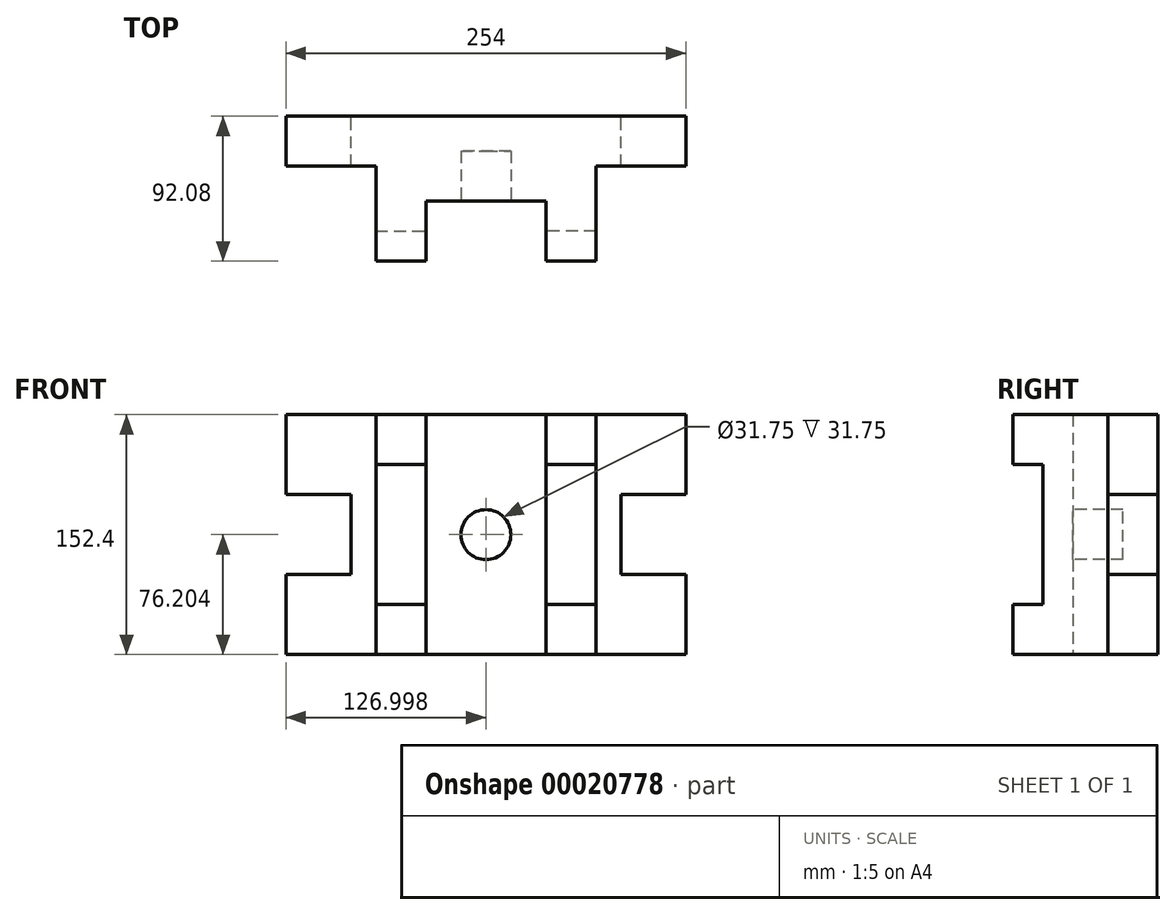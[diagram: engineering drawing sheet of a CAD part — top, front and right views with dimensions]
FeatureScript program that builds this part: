
annotation { "Feature Type Name" : "Feature", "Feature Type Description" : "" }
export const myFeature = defineFeature(function(context is Context, id is Id, definition is map)
    precondition{}
    {
        {
            var Q0;
            Q0=qCreatedBy(makeId("Front.planeOp"),FACE);
            var sketch = newSketch(context, id + "F0", { "sketchPlane" : qUnion([Q0])});
            skLineSegment(sketch, "E0.rect.bottom", {"start": v(31.56, -35.05) * mm, "end": v(-95.44, -35.05) * mm});
            skLineSegment(sketch, "E0.rect.top", {"start": v(-9.72, 41.15) * mm, "end": v(-95.44, 41.15) * mm});
            skLineSegment(sketch, "E0.rect.left", {"start": v(31.56, -35.05) * mm, "end": v(31.56, 15.75) * mm});
            skLineSegment(sketch, "E0.rect.right", {"start": v(-95.44, -35.05) * mm, "end": v(-95.44, 41.15) * mm});
            skPoint(sketch, "E0.rect.middle", {"position": v(-31.94, 3.05) * mm});
            skLineSegment(sketch, "E1.top", {"start": v(31.56, 15.75) * mm, "end": v(-9.72, 15.75) * mm});
            skLineSegment(sketch, "E1.right", {"start": v(-9.72, 41.15) * mm, "end": v(-9.72, 15.75) * mm});
            skPoint(sketch, "E2.orphan", {"position": v(31.56, 41.15) * mm});
            skSolve(sketch);
        }
        {
            var Q0;
            Q0=makeQuery(id+"F0.imprint","IMPRINT",FACE,{"disambiguationData":[TD([[makeQuery(id+"F0.imprint","IMPRINT",EDGE,{"derivedFrom":sQuery(id+"F0.wireOp",EDGE,"E0.rect.bottom")}),-1.0]])]});
            extrude(context, id + "F1", {"entities" : qUnion([Q0]), "depth" : 31.75 * mm});
        }
        {
            var Q0;
            Q0=makeQuery(id+"F1.opExtrude","CAP_FACE",FACE,{"disambiguationData":[OSD([sQuery(id+"F0.wireOp",EDGE,"E0.rect.bottom"),sQuery(id+"F0.wireOp",EDGE,"E0.rect.top"),sQuery(id+"F0.wireOp",EDGE,"E0.rect.left"),sQuery(id+"F0.wireOp",EDGE,"E0.rect.right"),sQuery(id+"F0.wireOp",EDGE,"E1.top"),sQuery(id+"F0.wireOp",EDGE,"E1.right")])],"isStart":false});
            var sketch = newSketch(context, id + "F2", { "sketchPlane" : qUnion([Q0])});
            skLineSegment(sketch, "E3.bottom", {"start": v(-95.44, -35.05) * mm, "end": v(-25.6, -35.05) * mm});
            skLineSegment(sketch, "E3.top", {"start": v(-95.44, 41.15) * mm, "end": v(-25.6, 41.15) * mm});
            skLineSegment(sketch, "E3.left", {"start": v(-95.44, -35.05) * mm, "end": v(-95.44, 41.15) * mm});
            skLineSegment(sketch, "E3.right", {"start": v(-25.6, -35.05) * mm, "end": v(-25.6, 41.15) * mm});
            skLineSegment(sketch, "E4.bottom", {"start": v(-25.6, -35.05) * mm, "end": v(-48.16, -35.05) * mm});
            skLineSegment(sketch, "E4.left", {"start": v(-25.6, -35.05) * mm, "end": v(-25.6, -11.85) * mm});
            skSolve(sketch);
        }
        {
            var Q0;
            Q0=makeQuery(id+"F2.imprint","IMPRINT",FACE,{"disambiguationData":[TD([[makeQuery(id+"F2.imprint","IMPRINT",EDGE,{"derivedFrom":sQuery(id+"F2.wireOp",EDGE,"E3.bottom")}),-1.0]])]});
            extrude(context, id + "F3", {"entities" : qUnion([Q0]), "operationType" : NewBodyOperationType.ADD, "depth" : 60.32 * mm});
        }
        {
            var Q0;
            Q0=makeQuery(id+"F3.opExtrude","CAP_FACE",FACE,{"disambiguationData":[OSD([sQuery(id+"F2.wireOp",EDGE,"E3.bottom"),sQuery(id+"F2.wireOp",EDGE,"E3.top"),sQuery(id+"F2.wireOp",EDGE,"E3.left"),sQuery(id+"F2.wireOp",EDGE,"E3.right"),sQuery(id+"F2.wireOp",EDGE,"E4.bottom"),sQuery(id+"F2.wireOp",EDGE,"E4.left")])],"isStart":false});
            var sketch = newSketch(context, id + "F4", { "sketchPlane" : qUnion([Q0])});
            skLineSegment(sketch, "E5.bottom", {"start": v(-25.6, -35.05) * mm, "end": v(-57.34, -35.05) * mm});
            skLineSegment(sketch, "E5.top", {"start": v(-25.6, -3.3) * mm, "end": v(-57.34, -3.3) * mm});
            skLineSegment(sketch, "E5.left", {"start": v(-25.6, -35.05) * mm, "end": v(-25.6, -3.3) * mm});
            skLineSegment(sketch, "E5.right", {"start": v(-57.34, -35.05) * mm, "end": v(-57.34, -3.3) * mm});
            skLineSegment(sketch, "E6", {"start": v(-57.34, -3.3) * mm, "end": v(-57.34, 41.15) * mm});
            skSolve(sketch);
        }
        {
            var Q0;
            {var subQ4=sQuery(id+"F4.wireOp",EDGE,"E5.top");Q0=makeQuery(id+"F4.imprint","IMPRINT",FACE,{"disambiguationData":[TD([[makeQuery(id+"F4.imprint","IMPRINT",EDGE,{"derivedFrom":subQ4}),-1.0]])]});}
            extrude(context, id + "F5", {"entities" : qUnion([Q0]), "operationType" : NewBodyOperationType.REMOVE, "oppositeDirection" : true, "depth" : 19.05 * mm});
        }
        {
            var Q0;
            Q0=makeQuery(id+"F3.opExtrude","CAP_FACE",FACE,{"disambiguationData":[OSD([sQuery(id+"F2.wireOp",EDGE,"E3.bottom"),sQuery(id+"F2.wireOp",EDGE,"E3.top"),sQuery(id+"F2.wireOp",EDGE,"E3.left"),sQuery(id+"F2.wireOp",EDGE,"E3.right"),sQuery(id+"F2.wireOp",EDGE,"E4.bottom"),sQuery(id+"F2.wireOp",EDGE,"E4.left")])],"isStart":false});
            var sketch = newSketch(context, id + "F6", { "sketchPlane" : qUnion([Q0])});
            skLineSegment(sketch, "E7", {"start": v(-57.34, -3.3) * mm, "end": v(-57.34, -35.05) * mm});
            skSolve(sketch);
        }
        {
            var Q0;
            {var subQ1=sQuery(id+"F6.wireOp",EDGE,"E7");Q0=makeQuery(id+"F6.imprint","IMPRINT",FACE,{"disambiguationData":[TD([[makeQuery(id+"F6.imprint","IMPRINT",EDGE,{"derivedFrom":subQ1}),-1.0]])]});}
            extrude(context, id + "F7", {"entities" : qUnion([Q0]), "operationType" : NewBodyOperationType.REMOVE, "oppositeDirection" : true, "depth" : 38.1 * mm});
        }
        {
            var Q0;
            Q0=makeQuery(id+"F1.opExtrude","SWEPT_BODY",BODY,{"disambiguationData":[OSD([sQuery(id+"F0.wireOp",EDGE,"E0.rect.bottom"),sQuery(id+"F0.wireOp",EDGE,"E0.rect.top"),sQuery(id+"F0.wireOp",EDGE,"E0.rect.left"),sQuery(id+"F0.wireOp",EDGE,"E0.rect.right"),sQuery(id+"F0.wireOp",EDGE,"E1.top"),sQuery(id+"F0.wireOp",EDGE,"E1.right")])]});
            var Q1;
            Q1=makeQuery(id+"F3.boolean.opBoolean","MERGE",FACE,{"derivedFrom":[makeQuery(id+"F1.opExtrude","SWEPT_FACE",FACE,{"disambiguationData":[OSD([sQuery(id+"F0.wireOp",EDGE,"E0.rect.top")])]}),makeQuery(id+"F3.opExtrude","SWEPT_FACE",FACE,{"disambiguationData":[OSD([sQuery(id+"F2.wireOp",EDGE,"E3.top")])]})]});
            mirror(context, id + "F8", {"operationType" : NewBodyOperationType.ADD, "entities" : qUnion([Q0]), "mirrorPlane" : qUnion([Q1])});
        }
        {
            var Q0;
            Q0=makeQuery(id+"F1.opExtrude","SWEPT_BODY",BODY,{"disambiguationData":[OSD([sQuery(id+"F0.wireOp",EDGE,"E0.rect.bottom"),sQuery(id+"F0.wireOp",EDGE,"E0.rect.top"),sQuery(id+"F0.wireOp",EDGE,"E0.rect.left"),sQuery(id+"F0.wireOp",EDGE,"E0.rect.right"),sQuery(id+"F0.wireOp",EDGE,"E1.top"),sQuery(id+"F0.wireOp",EDGE,"E1.right")])]});
            var Q1;
            {var subQ0=makeQuery(id+"F3.boolean.opBoolean","MERGE",FACE,{"derivedFrom":[makeQuery(id+"F1.opExtrude","SWEPT_FACE",FACE,{"disambiguationData":[OSD([sQuery(id+"F0.wireOp",EDGE,"E0.rect.right")])]}),makeQuery(id+"F3.opExtrude","SWEPT_FACE",FACE,{"disambiguationData":[OSD([sQuery(id+"F2.wireOp",EDGE,"E3.left")])]})]});Q1=makeQuery(id+"F8.boolean.opBoolean","MERGE",FACE,{"derivedFrom":[subQ0,makeQuery(id+"F8.opPattern","COPY",FACE,{"derivedFrom":subQ0,"instanceName":"1"})]});}
            mirror(context, id + "F9", {"operationType" : NewBodyOperationType.ADD, "entities" : qUnion([Q0]), "mirrorPlane" : qUnion([Q1])});
        }
        {
            var Q0;
            {var subQ0=makeQuery(id+"F7.boolean.opBoolean","COPY",FACE,{"derivedFrom":makeQuery(id+"F7.opExtrude","CAP_FACE",FACE,{"disambiguationData":[OSD([sQuery(id+"F2.wireOp",EDGE,"E3.bottom"),sQuery(id+"F2.wireOp",EDGE,"E3.top"),sQuery(id+"F2.wireOp",EDGE,"E3.left"),sQuery(id+"F2.wireOp",EDGE,"E4.bottom"),sQuery(id+"F4.wireOp",EDGE,"E6"),sQuery(id+"F6.wireOp",EDGE,"E7")])],"isStart":false})});var subQ1=makeQuery(id+"F8.boolean.opBoolean","MERGE",FACE,{"derivedFrom":[subQ0,makeQuery(id+"F8.opPattern","COPY",FACE,{"derivedFrom":subQ0,"instanceName":"1"})]});Q0=makeQuery(id+"F9.boolean.opBoolean","MERGE",FACE,{"derivedFrom":[subQ1,makeQuery(id+"F9.opPattern","COPY",FACE,{"derivedFrom":subQ1,"instanceName":"1"})]});}
            var sketch = newSketch(context, id + "F10", { "sketchPlane" : qUnion([Q0])});
            skCircle(sketch, "E8", {"center": v(-95.44, 41.15) * mm, "radius": 15.88 * mm});
            skPoint(sketch, "E9.orphan", {"position": v(-133.54, 117.35) * mm});
            skPoint(sketch, "E10.end.orphan", {"position": v(-57.34, -35.05) * mm});
            skSolve(sketch);
        }
        {
            var Q0;
            Q0=makeQuery(id+"F10.imprint","IMPRINT",FACE,{"disambiguationData":[TD([[makeQuery(id+"F10.imprint","IMPRINT",EDGE,{"derivedFrom":sQuery(id+"F10.wireOp",EDGE,"E8")}),1.0]])]});
            extrude(context, id + "F11", {"entities" : qUnion([Q0]), "operationType" : NewBodyOperationType.REMOVE, "oppositeDirection" : true, "depth" : 31.75 * mm});
        }
    });
